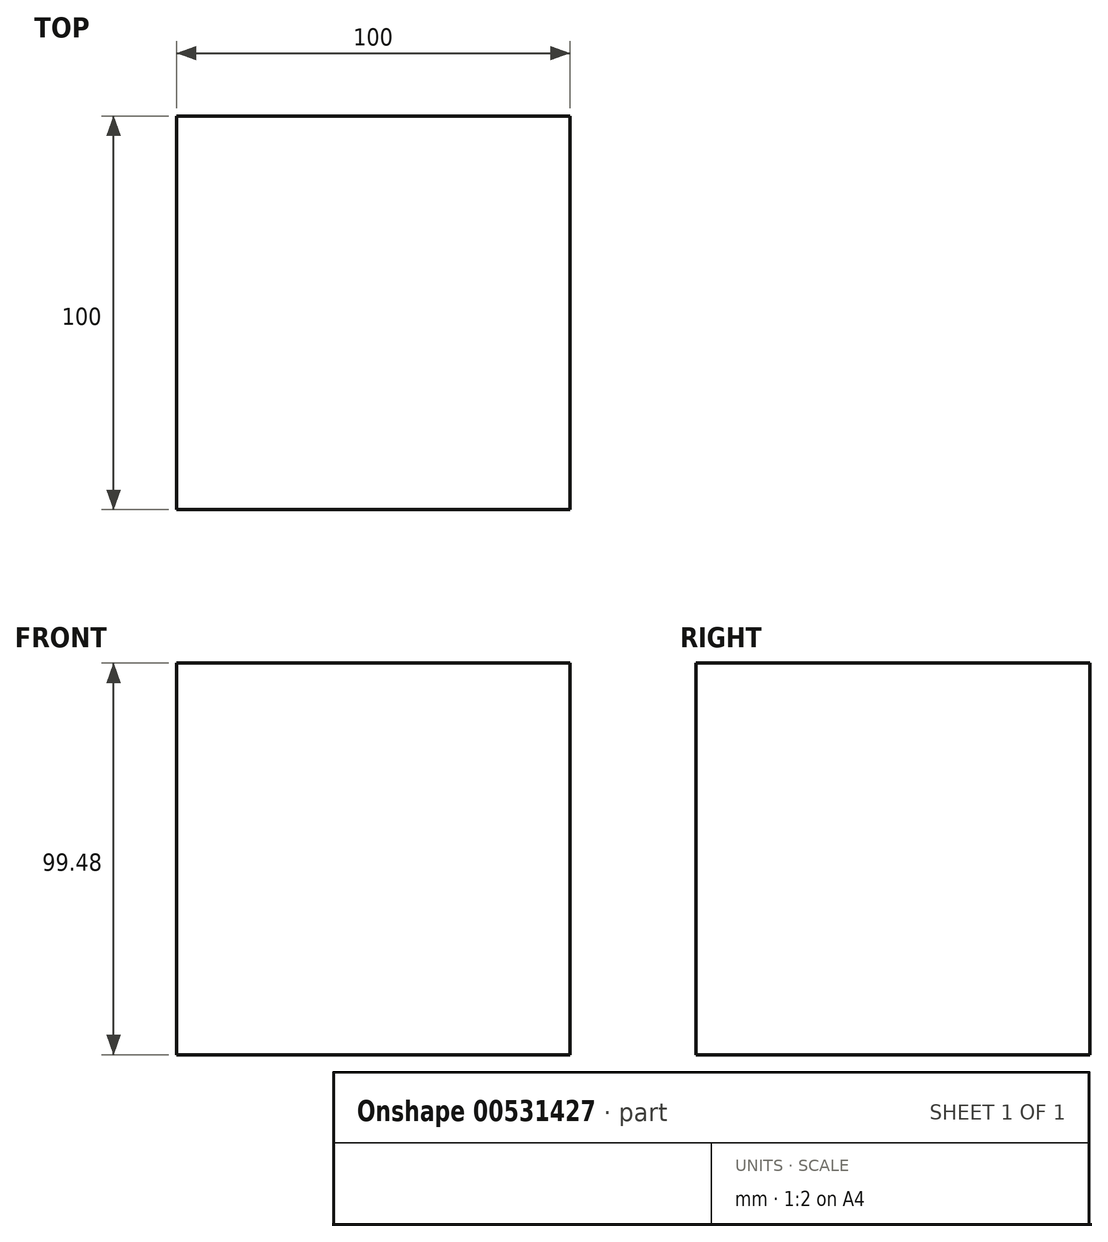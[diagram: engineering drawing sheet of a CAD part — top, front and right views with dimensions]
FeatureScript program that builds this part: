
annotation { "Feature Type Name" : "Feature", "Feature Type Description" : "" }
export const myFeature = defineFeature(function(context is Context, id is Id, definition is map)
    precondition{}
    {
        {
            var Q0;
            Q0=qCreatedBy(makeId("Front.planeOp"),FACE);
            var sketch = newSketch(context, id + "F0", { "sketchPlane" : qUnion([Q0])});
            skLineSegment(sketch, "E0.bottom", {"start": v(50, 49.74) * mm, "end": v(-50, 49.74) * mm});
            skLineSegment(sketch, "E0.top", {"start": v(50, -49.74) * mm, "end": v(-50, -49.74) * mm});
            skLineSegment(sketch, "E0.left", {"start": v(50, 49.74) * mm, "end": v(50, -49.74) * mm});
            skLineSegment(sketch, "E0.right", {"start": v(-50, 49.74) * mm, "end": v(-50, -49.74) * mm});
            skPoint(sketch, "E0.middle", {"position": v(0, 0) * mm});
            skLineSegment(sketch, "E1.bottom", {"start": v(50, 66.58) * mm, "end": v(-50, 66.58) * mm});
            skLineSegment(sketch, "E1.top", {"start": v(50, 53.95) * mm, "end": v(-50, 53.95) * mm});
            skLineSegment(sketch, "E1.left", {"start": v(50, 66.58) * mm, "end": v(50, 53.95) * mm});
            skLineSegment(sketch, "E1.right", {"start": v(-50, 66.58) * mm, "end": v(-50, 53.95) * mm});
            skPoint(sketch, "E1.middle", {"position": v(0, 60.26) * mm});
            skSolve(sketch);
        }
        {
            var Q0;
            Q0 = qSketchRegion(id + "F0", true);
            extrude(context, id + "F1", {"entities" : qUnion([Q0]), "endBound" : BoundingType.SYMMETRIC, "depth" : 100 * mm, "offsetDistance" : 25.4 * mm});
        }
        {
            var Q0;
            Q0=makeQuery(id+"F1.opExtrude","SWEPT_BODY",BODY,{"disambiguationData":[OSD([sQuery(id+"F0.wireOp",EDGE,"E1.bottom"),sQuery(id+"F0.wireOp",EDGE,"E1.top"),sQuery(id+"F0.wireOp",EDGE,"E1.left"),sQuery(id+"F0.wireOp",EDGE,"E1.right")])]});
            deleteBodies(context, id + "F2", {"entities" : qUnion([Q0])});
        }
    });
